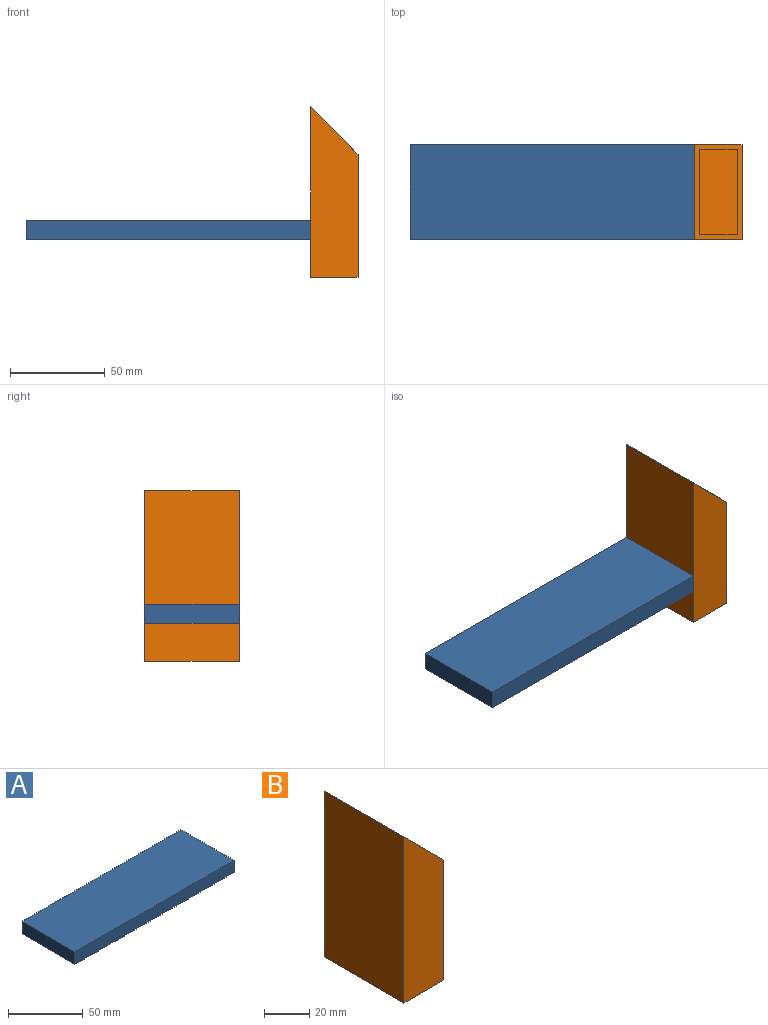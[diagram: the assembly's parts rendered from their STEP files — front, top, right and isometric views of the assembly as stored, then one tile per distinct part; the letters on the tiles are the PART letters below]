
ASSEMBLY  parts=2 mates=1
PART A: 6 faces, bbox 150x50x10 mm
  f0: plane 150x10mm, normal (0,1,0), area 1500mm2, adj f1,f3,f4,f5
  f1: plane 50x10mm, normal (-1,0,0), area 500mm2, adj f0,f2,f4,f5
  f2: plane 150x10mm, normal (0,-1,0), area 1500mm2, adj f1,f3,f4,f5
  f3: plane 50x10mm, normal (1,0,0), area 500mm2, adj f0,f2,f4,f5
  f4: plane 150x50mm, normal (0,0,1), area 7500mm2, adj f0,f1,f2,f3
  f5: plane 150x50mm, normal (0,0,-1), area 7500mm2, adj f0,f1,f2,f3
PART B: 11 faces, bbox 25x50x90 mm
  f0: plane 50x25mm, normal (0.71,0,0.71), area 495mm2, adj f2,f3,f4,f5,f7,f8,f9,f10
  f1: plane 50x25mm, normal (0,0,-1), area 1250mm2, adj f2,f3,f4,f5
  f2: plane 90x25mm, normal (0,1,0), area 1937.5mm2, adj f0,f1,f4,f5
  f3: plane 90x25mm, normal (0,-1,0), area 1937.5mm2, adj f0,f1,f4,f5
  f4: plane 90x50mm, normal (-1,0,0), area 4500mm2, adj f0,f1,f2,f3
  f5: plane 65x50mm, normal (1,0,0), area 3250mm2, adj f0,f1,f2,f3
  f6: plane 45x20mm, normal (0,0,1), area 900mm2, adj f7,f8,f9,f10
  f7: plane 85x20mm, normal (0,-1,0), area 1500mm2, adj f0,f6,f9,f10
  f8: plane 85x20mm, normal (0,1,0), area 1500mm2, adj f0,f6,f9,f10
  f9: plane 85x45mm, normal (1,0,0), area 3825mm2, adj f0,f6,f7,f8
  f10: plane 65x45mm, normal (-1,0,0), area 2925mm2, adj f0,f6,f7,f8
PLACE A t=(-184.62,-42.74,-6.46)mm
PLACE B t=(-178.14,-51.52,-6.46)mm
MATE fastened A.f3 <-> B.f4  axis (1,0,0) through (-123.14,-51.52,-6.46)mm
